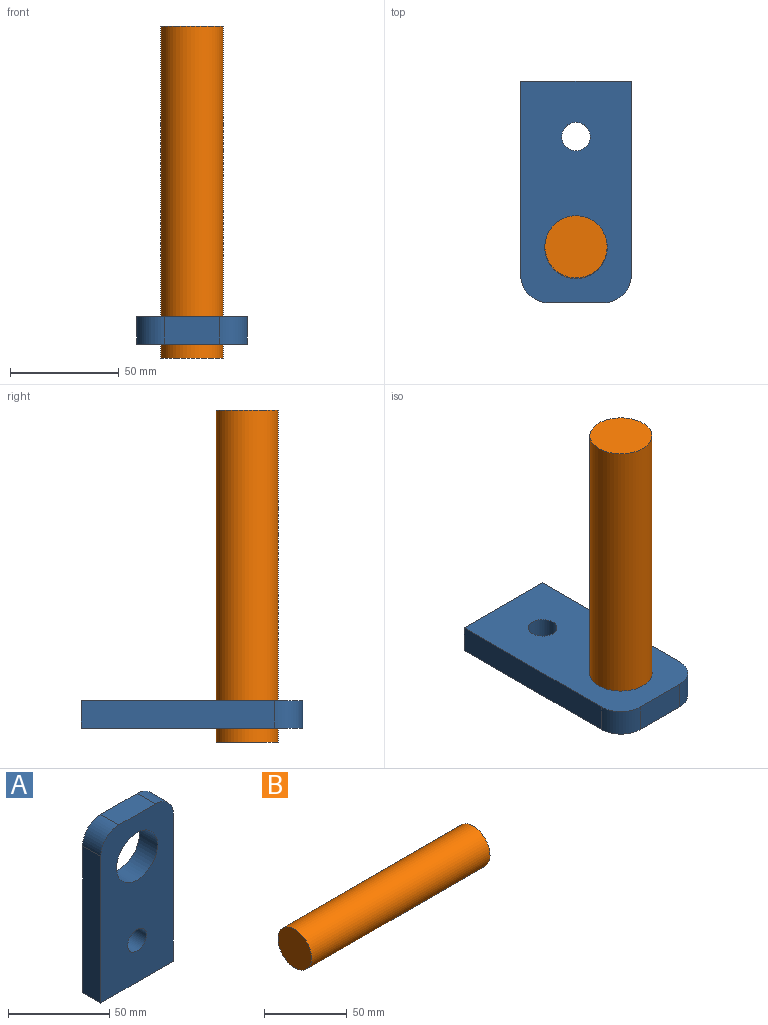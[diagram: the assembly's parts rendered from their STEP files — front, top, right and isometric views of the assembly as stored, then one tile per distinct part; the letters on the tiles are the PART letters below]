
ASSEMBLY  parts=2 mates=1
PART A: 10 faces, bbox 50.8x12.7x101.6 mm
  f0: plane 88.9x12.7mm, normal (1,0,0), area 1129mm2, adj f3,f4,f5,f7
  f1: plane 25.4x12.7mm, normal (0,0,1), area 322.6mm2, adj f4,f5,f7,f8
  f2: plane 88.9x12.7mm, normal (-1,0,0), area 1129mm2, adj f3,f4,f5,f8
  f3: plane 50.8x12.7mm, normal (0,0,-1), area 645.2mm2, adj f0,f2,f4,f5
  f4: plane 101.6x50.8mm, normal (0,-1,0), area 4310.3mm2, adj f0,f1,f2,f3,f6,f7,f8,f9
  f5: plane 101.6x50.8mm, normal (0,1,0), area 4310.3mm2, adj f0,f1,f2,f3,f6,f7,f8,f9
  f6: cylinder r=14.35mm len=28.7mm, axis (0,-1,0), area 1145.2mm2, adj f4,f5
  f7: cylinder r=12.7mm len=12.7mm, axis (0,-1,0), area 253.4mm2, adj f0,f1,f4,f5
  f8: cylinder r=12.7mm len=12.7mm, axis (0,1,0), area 253.4mm2, adj f1,f2,f4,f5
  f9: cylinder r=6.55mm len=13.1mm, axis (0,-1,0), area 522.5mm2, adj f4,f5
PART B: 3 faces, bbox 152.4x28.6x28.6 mm
  f0: plane 28.58x28.58mm, normal (-1,0,0), area 641.3mm2, adj f2
  f1: plane 28.58x28.58mm, normal (1,0,0), area 641.3mm2, adj f2
  f2: cylinder r=14.29mm len=152.4mm, axis (-1,0,0), area 13681.1mm2, adj f0,f1
PLACE A rot(axis=(1,0,0),90deg) t=(0,25.4,-6.35)mm
PLACE B rot(axis=(0,1,0),90deg) t=(0,0,57.15)mm
MATE fastened A.f6 <-> B.f2  axis (0,0,-1) through (0,0,-12.7)mm
